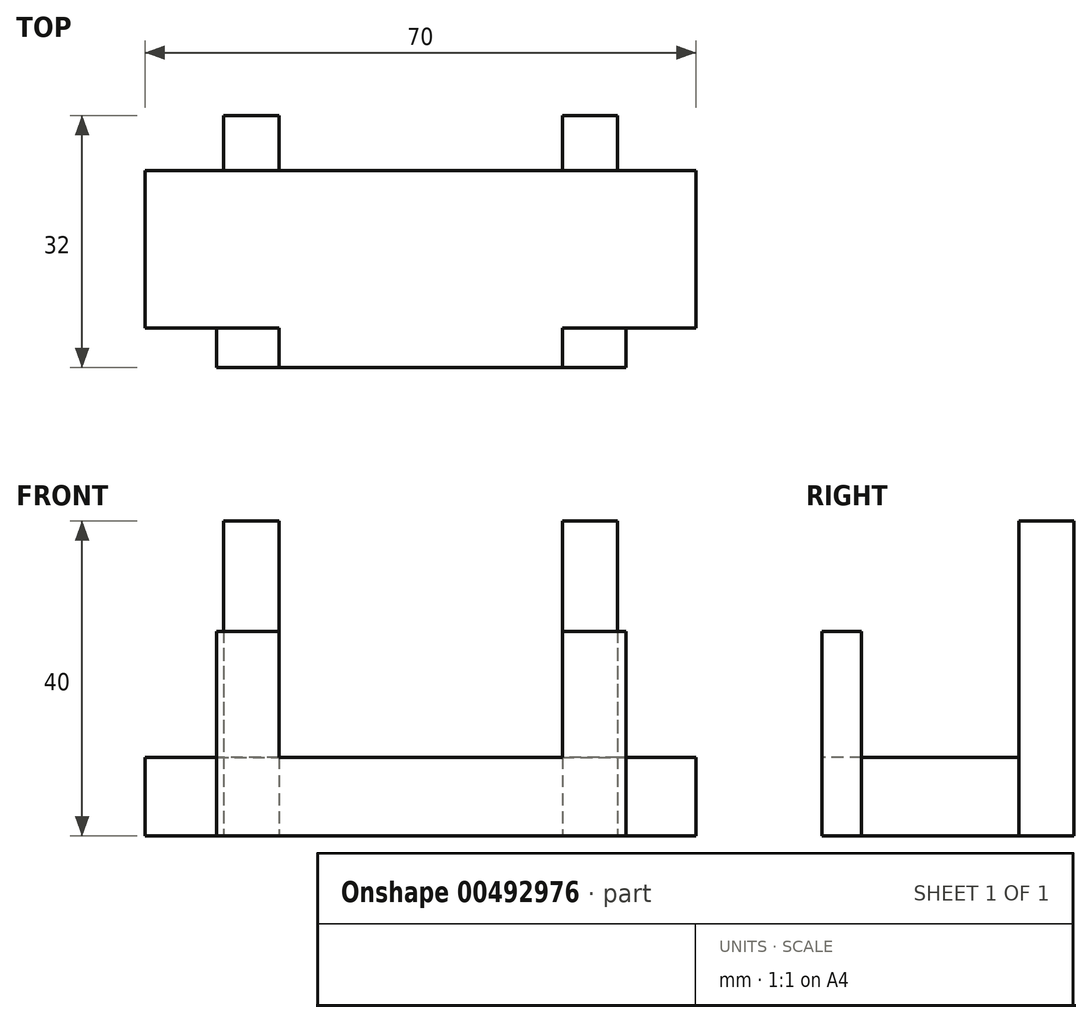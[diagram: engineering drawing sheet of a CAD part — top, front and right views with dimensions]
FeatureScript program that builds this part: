
annotation { "Feature Type Name" : "Feature", "Feature Type Description" : "" }
export const myFeature = defineFeature(function(context is Context, id is Id, definition is map)
    precondition{}
    {
        {
            var Q0;
            Q0=qCreatedBy(makeId("Top.planeOp"),FACE);
            var sketch = newSketch(context, id + "F0", { "sketchPlane" : qUnion([Q0])});
            skLineSegment(sketch, "E0.bottom", {"start": v(65.85, 22.37) * mm, "end": v(-4.15, 22.37) * mm});
            skLineSegment(sketch, "E0.top", {"start": v(65.85, 2.37) * mm, "end": v(-4.15, 2.37) * mm});
            skLineSegment(sketch, "E0.left", {"start": v(65.85, 22.37) * mm, "end": v(65.85, 2.37) * mm});
            skLineSegment(sketch, "E0.right", {"start": v(-4.15, 22.37) * mm, "end": v(-4.15, 2.37) * mm});
            skLineSegment(sketch, "E1.bottom", {"start": v(5.85, 22.37) * mm, "end": v(12.85, 22.37) * mm});
            skLineSegment(sketch, "E1.top", {"start": v(5.85, 29.37) * mm, "end": v(12.85, 29.37) * mm});
            skLineSegment(sketch, "E1.left", {"start": v(5.85, 22.37) * mm, "end": v(5.85, 29.37) * mm});
            skLineSegment(sketch, "E1.right", {"start": v(12.85, 22.37) * mm, "end": v(12.85, 29.37) * mm});
            skLineSegment(sketch, "E2.bottom", {"start": v(55.85, 22.37) * mm, "end": v(48.85, 22.37) * mm});
            skLineSegment(sketch, "E2.top", {"start": v(55.85, 29.37) * mm, "end": v(48.85, 29.37) * mm});
            skLineSegment(sketch, "E2.left", {"start": v(55.85, 22.37) * mm, "end": v(55.85, 29.37) * mm});
            skLineSegment(sketch, "E2.right", {"start": v(48.85, 22.37) * mm, "end": v(48.85, 29.37) * mm});
            skSolve(sketch);
        }
        {
            var Q0;
            Q0 = qSketchRegion(id + "F0", true);
            extrude(context, id + "F1", {"entities" : qUnion([Q0]), "depth" : 10 * mm});
        }
        {
            var Q0;
            Q0=makeQuery(id+"F1.opExtrude","CAP_FACE",FACE,{"disambiguationData":[OSD([sQuery(id+"F0.wireOp",EDGE,"E0.bottom"),sQuery(id+"F0.wireOp",EDGE,"E0.top"),sQuery(id+"F0.wireOp",EDGE,"E0.left"),sQuery(id+"F0.wireOp",EDGE,"E0.right"),sQuery(id+"F0.wireOp",EDGE,"E1.top"),sQuery(id+"F0.wireOp",EDGE,"E1.left"),sQuery(id+"F0.wireOp",EDGE,"E1.right"),sQuery(id+"F0.wireOp",EDGE,"E2.top"),sQuery(id+"F0.wireOp",EDGE,"E2.left"),sQuery(id+"F0.wireOp",EDGE,"E2.right")])],"isStart":false});
            var sketch = newSketch(context, id + "F2", { "sketchPlane" : qUnion([Q0])});
            skLineSegment(sketch, "E3", {"start": v(55.85, 22.37) * mm, "end": v(48.85, 22.37) * mm});
            skLineSegment(sketch, "E4", {"start": v(48.85, 22.37) * mm, "end": v(12.85, 22.37) * mm});
            skLineSegment(sketch, "E5", {"start": v(12.85, 22.37) * mm, "end": v(5.85, 22.37) * mm});
            skSolve(sketch);
        }
        {
            var Q0;
            Q0=makeQuery(id+"F2.imprint","IMPRINT",FACE,{"disambiguationData":[TD([[makeQuery(id+"F2.imprint","IMPRINT",EDGE,{"derivedFrom":sQuery(id+"F2.wireOp",EDGE,"E5")}),-1.0]])]});
            var Q1;
            Q1=makeQuery(id+"F2.imprint","IMPRINT",FACE,{"disambiguationData":[TD([[makeQuery(id+"F2.imprint","IMPRINT",EDGE,{"derivedFrom":sQuery(id+"F2.wireOp",EDGE,"E3")}),-1.0]])]});
            extrude(context, id + "F3", {"entities" : qUnion([Q0, Q1]), "operationType" : NewBodyOperationType.ADD, "depth" : 30 * mm});
        }
        {
            var Q0;
            Q0=makeQuery(id+"F1.opExtrude","SWEPT_FACE",FACE,{"disambiguationData":[OSD([sQuery(id+"F0.wireOp",EDGE,"E0.top")])]});
            var sketch = newSketch(context, id + "F4", { "sketchPlane" : qUnion([Q0])});
            skLineSegment(sketch, "E6.bottom", {"start": v(4.94, 0) * mm, "end": v(56.96, 0) * mm});
            skLineSegment(sketch, "E6.top", {"start": v(4.94, 10) * mm, "end": v(56.96, 10) * mm});
            skLineSegment(sketch, "E6.left", {"start": v(4.94, 0) * mm, "end": v(4.94, 10) * mm});
            skLineSegment(sketch, "E6.right", {"start": v(56.96, 0) * mm, "end": v(56.96, 10) * mm});
            skSolve(sketch);
        }
        {
            var Q0;
            Q0=makeQuery(id+"F4.imprint","IMPRINT",FACE,{"disambiguationData":[TD([[makeQuery(id+"F4.imprint","IMPRINT",EDGE,{"derivedFrom":sQuery(id+"F4.wireOp",EDGE,"E6.bottom")}),-1.0]])]});
            extrude(context, id + "F5", {"entities" : qUnion([Q0]), "operationType" : NewBodyOperationType.ADD, "depth" : 5 * mm});
        }
        {
            var Q0;
            Q0=makeQuery(id+"F5.boolean.opBoolean","MERGE",FACE,{"derivedFrom":[makeQuery(id+"F1.opExtrude","CAP_FACE",FACE,{"disambiguationData":[OSD([sQuery(id+"F0.wireOp",EDGE,"E0.bottom"),sQuery(id+"F0.wireOp",EDGE,"E0.top"),sQuery(id+"F0.wireOp",EDGE,"E0.left"),sQuery(id+"F0.wireOp",EDGE,"E0.right"),sQuery(id+"F0.wireOp",EDGE,"E1.top"),sQuery(id+"F0.wireOp",EDGE,"E1.left"),sQuery(id+"F0.wireOp",EDGE,"E1.right"),sQuery(id+"F0.wireOp",EDGE,"E2.top"),sQuery(id+"F0.wireOp",EDGE,"E2.left"),sQuery(id+"F0.wireOp",EDGE,"E2.right")])],"isStart":false}),makeQuery(id+"F5.opExtrude","SWEPT_FACE",FACE,{"disambiguationData":[OSD([sQuery(id+"F4.wireOp",EDGE,"E6.top")])]})]});
            var sketch = newSketch(context, id + "F6", { "sketchPlane" : qUnion([Q0])});
            skLineSegment(sketch, "E7", {"start": v(4.94, 2.37) * mm, "end": v(56.96, 2.37) * mm});
            skSolve(sketch);
        }
        {
            var Q0;
            Q0=makeQuery(id+"F6.imprint","IMPRINT",FACE,{"disambiguationData":[TD([[makeQuery(id+"F6.imprint","IMPRINT",EDGE,{"derivedFrom":sQuery(id+"F6.wireOp",EDGE,"E7")}),-1.0]])]});
            extrude(context, id + "F7", {"entities" : qUnion([Q0]), "operationType" : NewBodyOperationType.ADD, "depth" : 16 * mm});
        }
        {
            var Q0;
            {var subQ0=sQuery(id+"F4.wireOp",EDGE,"E6.top");Q0=makeQuery(id+"F7.boolean.opBoolean","MERGE",FACE,{"derivedFrom":[makeQuery(id+"F5.opExtrude","CAP_FACE",FACE,{"disambiguationData":[OSD([sQuery(id+"F4.wireOp",EDGE,"E6.bottom"),subQ0,sQuery(id+"F4.wireOp",EDGE,"E6.left"),sQuery(id+"F4.wireOp",EDGE,"E6.right")])],"isStart":false}),makeQuery(id+"F7.opExtrude","SWEPT_FACE",FACE,{"disambiguationData":[OSD([subQ0])]})]});}
            var sketch = newSketch(context, id + "F8", { "sketchPlane" : qUnion([Q0])});
            skLineSegment(sketch, "E8.bottom", {"start": v(12.85, 26) * mm, "end": v(48.85, 26) * mm});
            skLineSegment(sketch, "E8.top", {"start": v(12.85, 10) * mm, "end": v(48.85, 10) * mm});
            skLineSegment(sketch, "E8.left", {"start": v(12.85, 26) * mm, "end": v(12.85, 10) * mm});
            skLineSegment(sketch, "E8.right", {"start": v(48.85, 26) * mm, "end": v(48.85, 10) * mm});
            skSolve(sketch);
        }
        {
            var Q0;
            Q0=makeQuery(id+"F8.imprint","IMPRINT",FACE,{"disambiguationData":[TD([[makeQuery(id+"F8.imprint","IMPRINT",EDGE,{"derivedFrom":sQuery(id+"F8.wireOp",EDGE,"E8.bottom")}),1.0]])]});
            extrude(context, id + "F9", {"entities" : qUnion([Q0]), "operationType" : NewBodyOperationType.REMOVE, "oppositeDirection" : true, "depth" : 25 * mm});
        }
        {
            var Q0;
            Q0=makeQuery(id+"F8.imprint","IMPRINT",FACE,{"disambiguationData":[TD([[makeQuery(id+"F8.imprint","IMPRINT",EDGE,{"derivedFrom":sQuery(id+"F8.wireOp",EDGE,"E8.bottom")}),1.0]])]});
            extrude(context, id + "F10", {"entities" : qUnion([Q0]), "operationType" : NewBodyOperationType.REMOVE, "oppositeDirection" : true, "depth" : 25 * mm});
        }
    });
